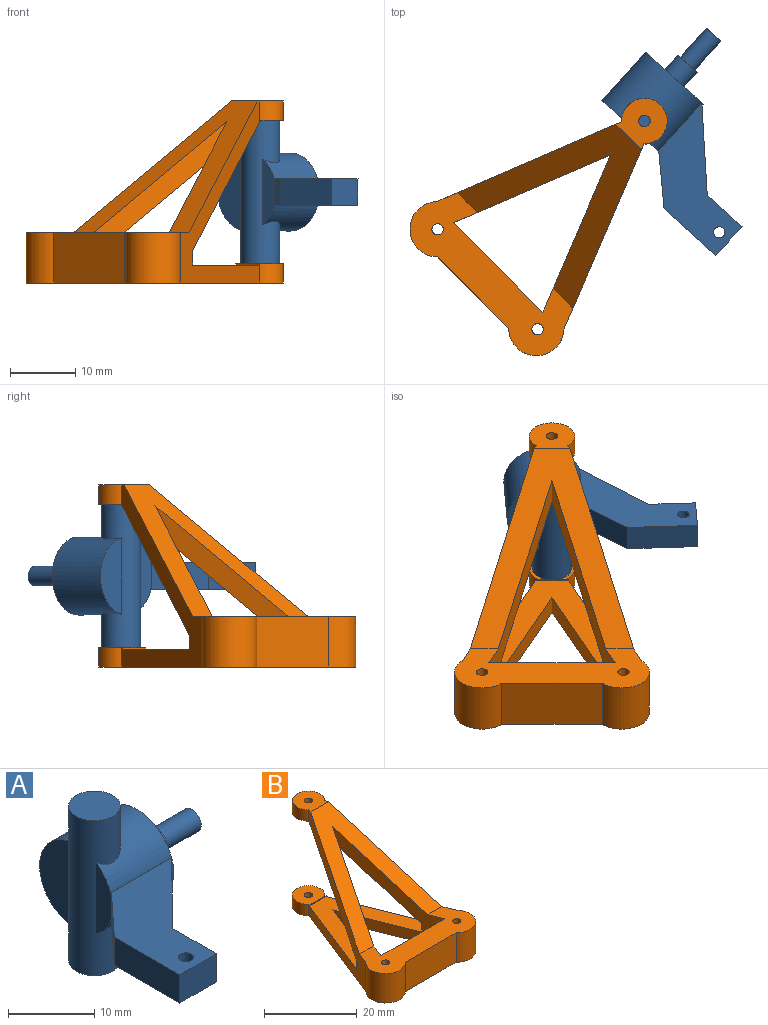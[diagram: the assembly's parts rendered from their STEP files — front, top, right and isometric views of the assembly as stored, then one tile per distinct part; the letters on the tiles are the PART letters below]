
ASSEMBLY  parts=2 mates=1
PART A: 21 faces, bbox 25x29x22 mm
  f0: cylinder r=6mm len=12mm, axis (-1,0,0), area 284.5mm2, adj f1,f2,f5,f6,f7,f8,f9,f10
  f1: plane 10.11x2.54mm, normal (-1,0,0), area 19.2mm2, adj f0,f2,f9
  f2: cylinder r=3mm len=22mm, axis (0,0,-1), area 265.4mm2, adj f0,f1,f3,f4,f5
  f3: plane 6x6mm, normal (0,0,1), area 28.3mm2, adj f2
  f4: plane 6x6mm, normal (0,0,-1), area 28.3mm2, adj f2
  f5: plane 11.74x4.76mm, normal (-1,0,0), area 41.8mm2, adj f0,f2
  f6: plane 12x12mm, normal (1,0,0), area 100.5mm2, adj f0,f17
  f7: plane 9.9x0.03mm, normal (0,1,0), area 0.3mm2, adj f0,f9,f10,f15
  f8: plane 9.9x0.03mm, normal (0,1,0), area 0.3mm2, adj f0,f9,f10,f16
  f9: plane 6.6x6.1mm, normal (-0.73,0.68,0), area 35.4mm2, adj f0,f1,f7,f8,f11,f15,f16
  f10: plane 10.15x10mm, normal (0.71,-0.7,0), area 55.8mm2, adj f0,f7,f8,f14,f15,f16
  f11: plane 10.73x4mm, normal (-1,0,0), area 42.9mm2, adj f9,f12,f15,f16
  f12: plane 6x4mm, normal (0,-1,0), area 24mm2, adj f11,f14,f15,f16
  f13: cylinder r=0.88mm len=4mm, axis (0,0,-1), area 22mm2, adj f15,f16
  f14: plane 7.18x4mm, normal (1,0,0), area 28.7mm2, adj f10,f12,f15,f16
  f15: plane 17.33x16mm, normal (0,0,1), area 132.2mm2, adj f7,f9,f10,f11,f12,f13,f14
  f16: plane 17.33x16mm, normal (0,0,-1), area 132.2mm2, adj f8,f9,f10,f11,f12,f13,f14
  f17: cylinder r=2mm len=4mm, axis (-1,0,0), area 37.7mm2, adj f6,f18
  f18: plane 4x4mm, normal (1,0,0), area 5.5mm2, adj f17,f19
  f19: cylinder r=1.5mm len=6mm, axis (-1,0,0), area 56.5mm2, adj f18,f20
  f20: plane 3x3mm, normal (1,0,0), area 7.1mm2, adj f19
PART B: 27 faces, bbox 30x42x28 mm
  f0: plane 25.11x24.66mm, normal (0,-0.63,0.77), area 266.9mm2, adj f1,f7,f12,f15,f24,f25
  f1: plane 30x10.4mm, normal (0,0,1), area 197.6mm2, adj f0,f7,f8,f9,f10,f11,f12,f14
  f2: plane 24.39x24.04mm, normal (0,0.63,-0.77), area 259.1mm2, adj f3,f6,f7,f12,f19,f22,f24,f25
  f3: plane 4.34x0.08mm, normal (0,0,-1), area 0.3mm2, adj f2,f4,f12,f24
  f4: plane 4.3x2.2mm, normal (0,1,0), area 9.4mm2, adj f3,f5,f12,f24
  f5: plane 24.1x24mm, normal (0,0,1), area 198.5mm2, adj f4,f7,f12,f20,f21,f24,f25
  f6: cylinder r=3.5mm len=7mm, axis (0,0,-1), area 50.1mm2, adj f2,f7,f12,f15,f22
  f7: plane 28.79x28mm, normal (-0.93,0.37,0), area 211.9mm2, adj f0,f1,f2,f5,f6,f8,f15,f16
  f8: cylinder r=4.25mm len=7.74mm, axis (0,0,-1), area 102.5mm2, adj f1,f7,f9,f18
  f9: plane 15.48x7.74mm, normal (0,-1,0), area 119.8mm2, adj f1,f8,f10,f18
  f10: cylinder r=4.25mm len=7.74mm, axis (0,0,-1), area 102.5mm2, adj f1,f9,f12,f18
  f11: cylinder r=0.88mm len=7.74mm, axis (0,0,-1), area 42.6mm2, adj f1,f18
  f12: plane 28.79x28mm, normal (0.93,0.37,0), area 211.9mm2, adj f0,f1,f2,f3,f4,f5,f6,f10
  f13: cylinder r=0.88mm len=3mm, axis (0,0,-1), area 16.5mm2, adj f15,f22
  f14: cylinder r=0.88mm len=7.74mm, axis (0,0,-1), area 42.6mm2, adj f1,f18
  f15: plane 7x6.94mm, normal (0,0,1), area 37.5mm2, adj f0,f6,f7,f12,f13
  f16: cylinder r=3.5mm len=7mm, axis (0,0,-1), area 50.1mm2, adj f7,f12,f18,f23
  f17: cylinder r=0.88mm len=3mm, axis (0,0,-1), area 16.5mm2, adj f18,f23
  f18: plane 42x30mm, normal (0,0,-1), area 441.4mm2, adj f7,f8,f9,f10,f11,f12,f14,f16
  f19: plane 4.34x0.08mm, normal (0,0,-1), area 0.3mm2, adj f2,f7,f20,f25
  f20: plane 4.3x2.2mm, normal (0,1,0), area 9.4mm2, adj f5,f7,f19,f25
  f21: plane 5.03x0.23mm, normal (0,-1,0), area 1.2mm2, adj f5,f7,f12,f23
  f22: plane 7x5.85mm, normal (0,0,-1), area 32mm2, adj f2,f6,f13
  f23: plane 7x6.33mm, normal (0,0,1), area 34.3mm2, adj f7,f12,f16,f17,f21
  f24: plane 24.8x24.46mm, normal (-0.93,-0.37,0), area 181.8mm2, adj f0,f1,f2,f3,f4,f5,f18,f25
  f25: plane 24.8x24.46mm, normal (0.93,-0.37,0), area 181.8mm2, adj f0,f1,f2,f5,f18,f19,f20,f24
  f26: plane 19.44x7.74mm, normal (0,1,0), area 150.5mm2, adj f1,f18,f24,f25
PLACE A rot(axis=(0,0,1),48deg) t=(1.23,57.04,5.14)mm
PLACE B rot(axis=(0,0,-1),45deg) t=(-22.99,32.82,2.14)mm
MATE revolute B.f6 <-> A.f2  axis (0,0,-1) through (1.23,57.04,27.14)mm
